# Revit family: RN 33171 Verteilventil
name_source: partatom
category: Rohrzubehör
units: mm (PartAtom-declared; Revit-internal decimal feet)

## family parameters
Arbeitsebenenbasiert = Nein
Beim Laden mit Abzugskörper schneiden = Nein
Bemaßung runder Anschluss = Durchmesser verwenden
Gemeinsam genutzt = Nein
Immer vertikal = Ja
Teiletyp = Ventil - Zerlegung in

## types (1)
- DN 20
    1.010.00.2 Blattnummer der Richtlinie = 17
    1.010.00.3 Ausgabedatum (Monat) der Richtlinie = 201601
    1.010.00.4 Herstellername = R. Nussbaum AG
    1.010.00.5 Revisionsdatum der Datei = 20190528
    1.010.00.6 Webadresse des Herstellers = http://www.nussbaum.ch
    1.100.00.3 Sortiernummer für Anzeigereihenfolge = 1
    1.100.00.4 Produktbezeichnung = Absperrarmaturen
    1.800.00.3 TGA-Nummer = 00106900000000000000000000000200700000000000000001???00000
    1.810.00.3 Hersteller-Bestellnummer = 33171.21
    1.810.00.4 DATANORM-Nummer = 33171.21
    1.810.00.6 GTIN-Nummer = 7612945743626
    1.960/3L.00.8 Link (URL) = https://www.nussbaum.ch
    17.700.00.30 Produktbeschreibung = 33171.21, Verteilventil, ohne Anschlussverschraubung, DN=20
    17.700.00.4 Armaturentyp = 1
    17.700.00.5 Nennweite DN = 20
    17.700.00.6 kvs-Wert [m3/h] = 6
    17.700.00.7 Maximale Betriebstemperatur TB [°C] = 90
    17.700.00.8 Maximaler Betriebsdruck (Arbeitsdruck) ps [1.0 · 105 Pa] = 16
    CONNECTOR0_DIAMETER_dZ_0r = 32 mm
    CONNECTOR0_dZ_00 = 51 mm
    CONNECTOR0_dZ_01 = 41 mm
    CONNECTOR0_ref_dZ = 41 mm
    CONNECTOR1_DIAMETER_dZ_0r = 25 mm  [stored 0.082021 ft]
    CONNECTOR1_dZ_00 = 42 mm  [stored 0.137795 ft]
    CONNECTOR1_dZ_01 = 59 mm
    CONNECTOR1_ref_dZ = 42 mm  [stored 0.137795 ft]
    CONNECTOR2_DIAMETER_dX_0r = 25 mm  [stored 0.082021 ft]
    CONNECTOR2_dX_00 = 43 mm
    CONNECTOR2_dX_01 = 60 mm  [stored 0.19685 ft]
    CONNECTOR2_ref_dX = 43 mm
    CONNECTOR2_ref_dZ = 1 mm  [stored 0.00328084 ft]
    Connector Visibility = Nein
    EnclosingSpace Visibility = Nein
    Hersteller = R. Nussbauzm AG
    Modell = 33171.21
    R. Nussbaum AG 33171.21 de Visibility = Ja
    Typenkommentare = VerteilventilDN 20
    URL = https://www.nussbaum.ch

note: [stored X ft] marks values corroborated as IEEE doubles in the binary element streams (Revit-internal decimal feet)

## geometry (parser evidence)
native form markers: Sweep x2
no freeform markers — native parametric forms only
